# Revit family: Schneider_D-Life_5-elementos
name_source: partatom
category: Electrical Fixtures
revit_build: Autodesk Revit 2015 (Build: 20160512_1515(x64)
units: mm (PartAtom-declared; Revit-internal decimal feet)

## types (1)
- Estándar
    Autor = A3D Consulting
    Autor.URL = www.a3d.es
    Default Elevation = 1000 mm  [stored 3.28084 ft]
    Elemento1.Tipo = Schneider_D-Life_Mecanismo-Tecla_Accesorios-Zumbador : Timbre-Ártico
    Elemento2.Tipo = Schneider_D-Life_Mecanismo-Tecla_Accesorios-Zumbador : Timbre-Ártico
    Elemento3.Tipo = Schneider_D-Life_Mecanismo-Tecla_Accesorios-Zumbador : Timbre-Ártico
    Elemento4.Tipo = Schneider_D-Life_Mecanismo-Tecla_Accesorios-Zumbador : Timbre-Ártico
    Elemento5.Tipo = Schneider_D-Life_Mecanismo-Tecla_Accesorios-Zumbador : Timbre-Ártico
    Marco.Tipo = Schneider_D-Life_Marco_5-elementos : Ártico
    Modelado por = 034
    Modificado por = 000
    Revisado por = 000
    Tecla.Anchura = 70 mm  [stored 0.229659 ft]
    Vacío.Espesor = 30 mm  [stored 0.0984252 ft]
    Versión = L2.00

note: [stored X ft] marks values corroborated as IEEE doubles in the binary element streams (Revit-internal decimal feet)

## geometry (parser evidence)
native form markers: Sweep x7
no freeform markers — native parametric forms only
